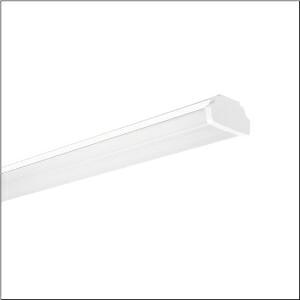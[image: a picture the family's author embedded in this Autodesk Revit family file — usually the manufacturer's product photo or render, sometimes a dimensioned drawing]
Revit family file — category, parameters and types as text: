
# Revit family: modario_r__31_mo_53bm812d2v4085_43f6
name_source: partatom
category: Lighting Fixtures
units: mm (PartAtom-declared; Revit-internal decimal feet)

## family parameters
Cut with Voids When Loaded = No
Host = Face
Light Source = No
Part Type = Normal
Room Calculation Point = No
Round Connector Dimension = Use Diameter
Shared = No

## types (1)
- --- (1 x LED, 8930 lm, 61.8 W, 4000K)
    Apparent Load = 62 VA
    CIE Flux Codes = 47 80 95 92 100
    Color Rendering = 80
    Color Temperature = 4000K
    Default Elevation = 1800 mm
    Description = Modario® 31 MO, luminaire insert, of sheet steel, coil coated, white, length: 1.495mm, width: 81mm, height: 82mm, 5x system unit, system units: 299mm, LED rated luminous flux: 8.930lm, light colour: 840, control gear: DALI 2, control gear: ECG DALI, with plug, 5-pole, with phase selection, mains connection: 220..240V, AC, 50/60Hz, rated input power: 62W, through-wiring accessed according to module size, primary optical cover: cover, of PMMA, light emission: direct distribution, primary light characteristic: symmetric, protection rating (complete): IP20, protection rating (LED compartment): IP50, insulation class (complete): insulation class I (protective earthing), certification: CE, ENEC, VDE, UKCA, impact resistance: IK03, permissible ambient temperature for indoor applications: -25..+30°C, corresponds to IFS (International Featured Standards) requirements for safety and quality in the food industry, reducing of maximum allowable ambient temperature of 5°C with ceiling mounting, packaging unit: 1 piece
    Height = 92 mm
    Lamp = 1 x LED
    Lamp Light Flux = 8930 lm
    Lamp Power = 61.8 W
    Lamp count = 1
    Length = 1495 mm
    Luminous efficacy = 145 lm/W
    Manufacturer = Siteco
    ModVariant = No
    Model = 53BM812D2V4085
    Mounting Place = Ceiling
    Mounting Type = Pendant
    Number of Poles = 1
    OnlyDefault = Yes
    Power Factor = 1
    Product Name = Modario® 31 MO
    Product group = luminaire insert
    ProductGroupID = 901
    Protection Class = Protection class I
    Protection Degree = IP 20
    RLX_Detail_Level = 1
    RLX_Emergency_Light_Flux = 0 lm
    RLX_Emergency_Type = 0
    RLX_Emergency_Type_DB = No
    RlxData = <blob elided: 42285 chars, md5=74077e0e>
    Socket = socket
    Standby Power = 0 W
    System Light Flux = 8930 lm
    System Power = 62 W
    Type Comments = factory setting: luminous flux: 100 % | dim-lin: 254 | 500 mA
    Type Image = l_1300283.jpg
    URL = http://relux.com
    VarID = @adj_130779
    Voltage = 0 V
    Weight = 0.00 kg
    Width = 81 mm

## geometry (parser evidence)
native form markers: Blend x4, Sweep x11
no freeform markers — native parametric forms only
